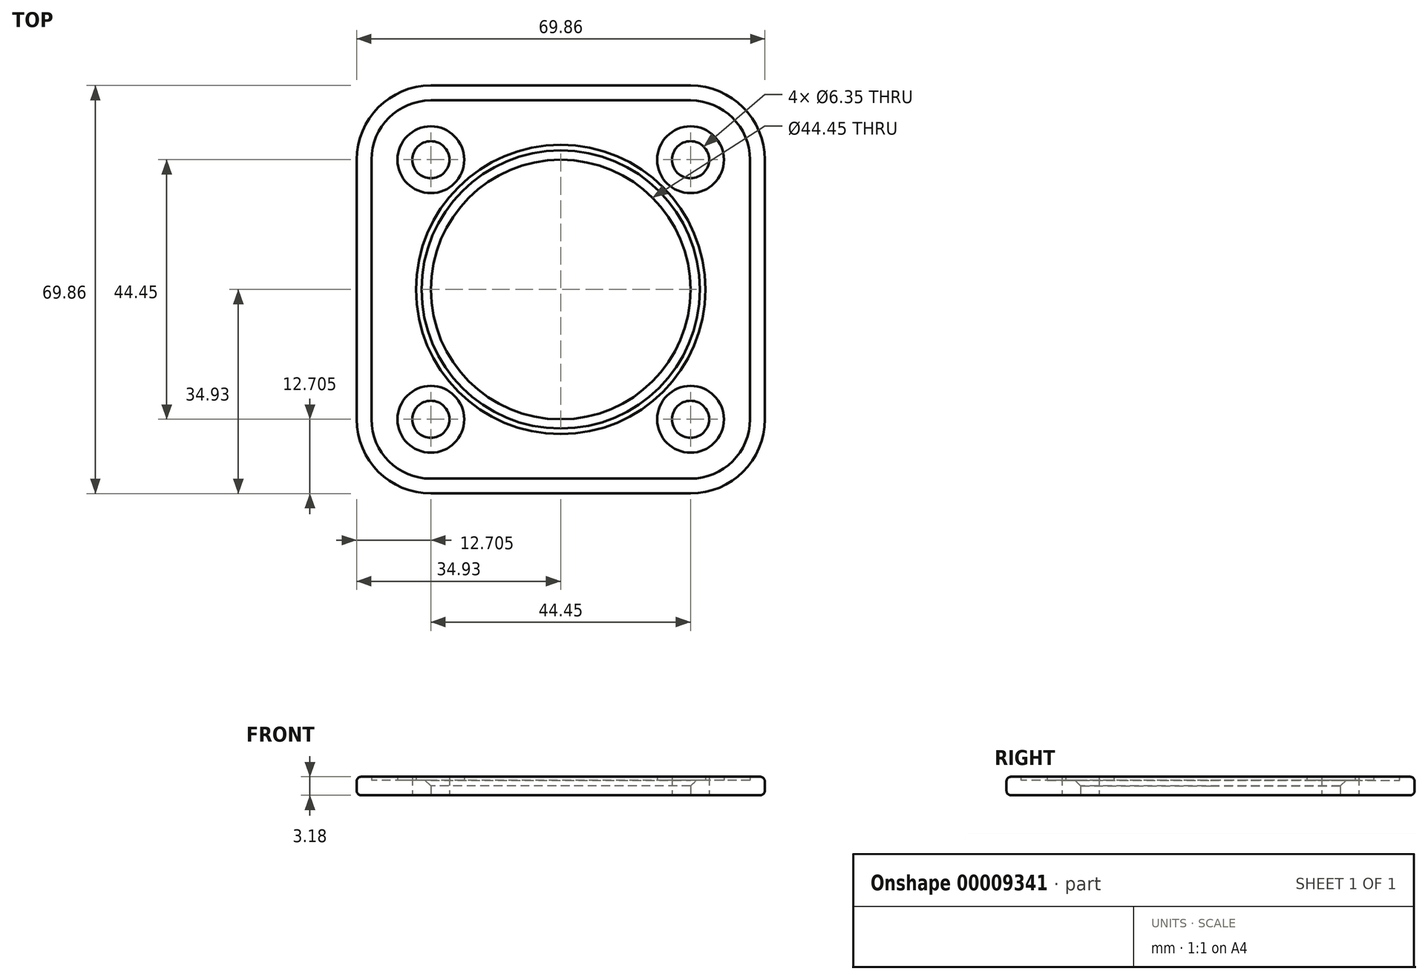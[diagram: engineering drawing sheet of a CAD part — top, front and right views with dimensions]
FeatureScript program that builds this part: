
annotation { "Feature Type Name" : "Feature", "Feature Type Description" : "" }
export const myFeature = defineFeature(function(context is Context, id is Id, definition is map)
    precondition{}
    {
        {
            var Q0;
            Q0=qCreatedBy(makeId("Top.planeOp"),FACE);
            var sketch = newSketch(context, id + "F0", { "sketchPlane" : qUnion([Q0])});
            skCircle(sketch, "E0", {"center": v(0, 0) * mm, "radius": 22.23 * mm});
            skLineSegment(sketch, "E1.rect.bottom", {"start": v(-22.23, 34.93) * mm, "end": v(22.23, 34.93) * mm});
            skLineSegment(sketch, "E1.rect.top", {"start": v(-22.23, -34.93) * mm, "end": v(22.23, -34.93) * mm});
            skLineSegment(sketch, "E1.rect.left", {"start": v(-34.93, 22.22) * mm, "end": v(-34.93, -22.23) * mm});
            skLineSegment(sketch, "E1.rect.right", {"start": v(34.93, 22.23) * mm, "end": v(34.93, -22.23) * mm});
            skCircle(sketch, "E2", {"center": v(-22.23, 22.23) * mm, "radius": 3.18 * mm});
            skCircle(sketch, "E3.0.1.0", {"center": v(-22.22, -22.23) * mm, "radius": 3.18 * mm});
            skCircle(sketch, "E3.1.0.0", {"center": v(22.22, 22.23) * mm, "radius": 3.18 * mm});
            skCircle(sketch, "E3.1.1.0", {"center": v(22.23, -22.23) * mm, "radius": 3.18 * mm});
            skLineSegment(sketch, "E3.direction1", {"start": v(-22.23, 22.23) * mm, "end": v(22.22, 22.23) * mm, "construction": true});
            skLineSegment(sketch, "E3.direction2", {"start": v(-22.23, 22.23) * mm, "end": v(-22.22, -22.23) * mm, "construction": true});
            skPoint(sketch, "E4.visualSharp", {"position": v(-34.93, 34.93) * mm});
            skArc(sketch, "E4.filletArc", {"start": v(-22.23, 34.92) * mm, "mid": v(-31.2, 31.2) * mm, "end": v(-34.93, 22.22) * mm});
            skPoint(sketch, "E5.visualSharp", {"position": v(34.93, 34.93) * mm});
            skArc(sketch, "E5.filletArc", {"start": v(34.93, 22.23) * mm, "mid": v(31.2, 31.2) * mm, "end": v(22.23, 34.93) * mm});
            skPoint(sketch, "E6.visualSharp", {"position": v(34.93, -34.93) * mm});
            skArc(sketch, "E6.filletArc", {"start": v(22.23, -34.93) * mm, "mid": v(31.2, -31.2) * mm, "end": v(34.93, -22.23) * mm});
            skPoint(sketch, "E7.visualSharp", {"position": v(-34.93, -34.93) * mm});
            skArc(sketch, "E7.filletArc", {"start": v(-34.93, -22.22) * mm, "mid": v(-31.2, -31.2) * mm, "end": v(-22.23, -34.93) * mm});
            skSolve(sketch);
        }
        {
            var Q0;
            Q0=makeQuery(id+"F0.imprint","IMPRINT",FACE,{"disambiguationData":[TD([[makeQuery(id+"F0.imprint","IMPRINT",EDGE,{"derivedFrom":sQuery(id+"F0.wireOp",EDGE,"E0")}),-1.0]])]});
            extrude(context, id + "F1", {"entities" : qUnion([Q0]), "depth" : 3.17 * mm});
        }
        {
            var Q0;
            Q0=makeQuery(id+"F1.opExtrude","CAP_FACE",FACE,{"disambiguationData":[OSD([sQuery(id+"F0.wireOp",EDGE,"E0"),sQuery(id+"F0.wireOp",EDGE,"E1.rect.bottom"),sQuery(id+"F0.wireOp",EDGE,"E1.rect.top"),sQuery(id+"F0.wireOp",EDGE,"E1.rect.left"),sQuery(id+"F0.wireOp",EDGE,"E1.rect.right"),sQuery(id+"F0.wireOp",EDGE,"E2"),sQuery(id+"F0.wireOp",EDGE,"E3.0.1.0"),sQuery(id+"F0.wireOp",EDGE,"E3.1.0.0"),sQuery(id+"F0.wireOp",EDGE,"E3.1.1.0"),sQuery(id+"F0.wireOp",EDGE,"E4.filletArc"),sQuery(id+"F0.wireOp",EDGE,"E5.filletArc"),sQuery(id+"F0.wireOp",EDGE,"E6.filletArc"),sQuery(id+"F0.wireOp",EDGE,"E7.filletArc")])],"isStart":false});
            shell(context, id + "F2", {"entities" : qUnion([Q0]), "thickness" : 2.54 * mm});
        }
        {
            var Q0;
            Q0=makeQuery(id+"F1.opExtrude","CAP_EDGE",EDGE,{"disambiguationData":[OSD([sQuery(id+"F0.wireOp",EDGE,"E0")])],"isStart":false});
            chamfer(context, id + "F3", {"entities" : qUnion([Q0]), "width" : 1.59 * mm, "tangentPropagation" : true});
        }
        {
            var Q0;
            Q0=makeQuery(id+"F1.opExtrude","CAP_EDGE",EDGE,{"disambiguationData":[OSD([sQuery(id+"F0.wireOp",EDGE,"E1.rect.top")])],"isStart":true});
            var Q1;
            Q1=makeQuery(id+"F1.opExtrude","CAP_EDGE",EDGE,{"disambiguationData":[OSD([sQuery(id+"F0.wireOp",EDGE,"E1.rect.top")])],"isStart":false});
            fillet(context, id + "F4", {"entities" : qUnion([Q0, Q1]), "radius" : 0.8 * mm, "tangentPropagation" : true, "allowEdgeOverflow" : false});
        }
    });
